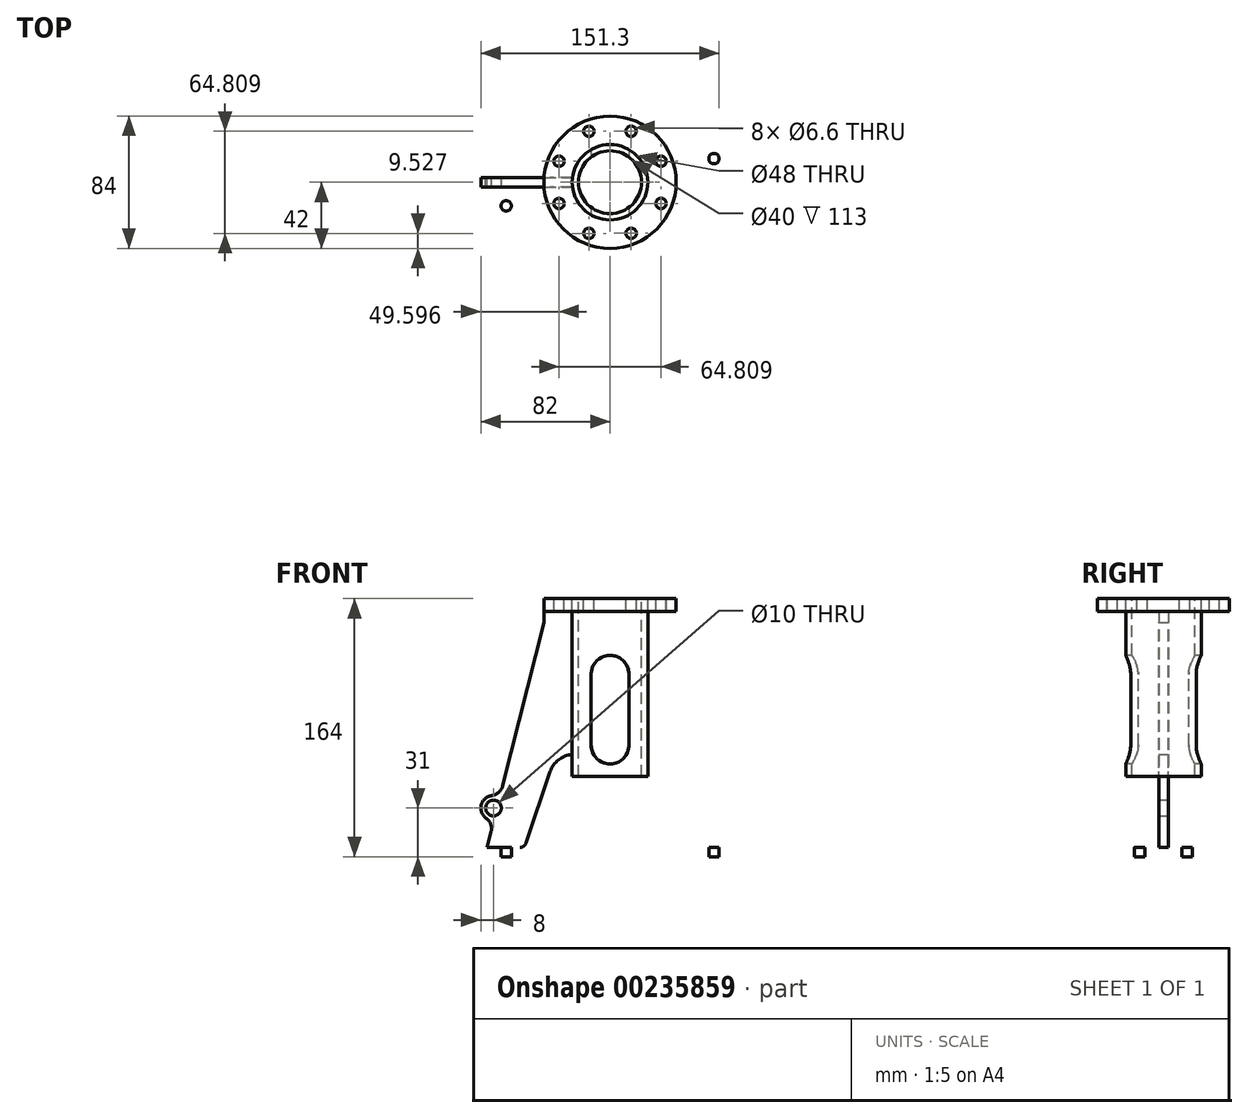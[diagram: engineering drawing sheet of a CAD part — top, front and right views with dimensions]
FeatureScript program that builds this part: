
annotation { "Feature Type Name" : "Feature", "Feature Type Description" : "" }
export const myFeature = defineFeature(function(context is Context, id is Id, definition is map)
    precondition{}
    {
        {
            var Q0;
            Q0=qCreatedBy(makeId("Front.planeOp"),FACE);
            var sketch = newSketch(context, id + "F0", { "sketchPlane" : qUnion([Q0])});
            skLineSegment(sketch, "E0.0", {"start": v(-42, 0) * mm, "end": v(-42, -8) * mm});
            skLineSegment(sketch, "E1.0", {"start": v(42, 0) * mm, "end": v(42, -8) * mm});
            skLineSegment(sketch, "E2", {"start": v(-42, 0) * mm, "end": v(42, 0) * mm});
            skLineSegment(sketch, "E3.0", {"start": v(-42, -8) * mm, "end": v(42, -8) * mm});
            skLineSegment(sketch, "E4", {"start": v(0, 0) * mm, "end": v(0, -4.96) * mm});
            skLineSegment(sketch, "E5", {"start": v(-78, -158) * mm, "end": v(-75.5, -148) * mm});
            skLineSegment(sketch, "E6.trimOffspring", {"start": v(-78, -158) * mm, "end": v(-78, -164) * mm});
            skCircle(sketch, "E7", {"center": v(-74, -133) * mm, "radius": 5 * mm});
            skArc(sketch, "E8", {"start": v(-75, -125.06) * mm, "mid": v(-81.76, -131.05) * mm, "end": v(-78.63, -139.53) * mm});
            skLineSegment(sketch, "E9.trimOffspring", {"start": v(-68.24, -119.08) * mm, "end": v(-42, -15) * mm});
            skPoint(sketch, "E10.visualSharp", {"position": v(-70, -126.07) * mm});
            skArc(sketch, "E10.filletArc", {"start": v(-75, -125.06) * mm, "mid": v(-70.7, -123.12) * mm, "end": v(-68.24, -119.08) * mm});
            skPoint(sketch, "E11.visualSharp", {"position": v(-73.73, -141) * mm});
            skArc(sketch, "E11.filletArc", {"start": v(-75.5, -148) * mm, "mid": v(-75.75, -143.28) * mm, "end": v(-78.63, -139.53) * mm});
            skArc(sketch, "E12", {"start": v(0, -36) * mm, "mid": v(-8.49, -39.51) * mm, "end": v(-12, -48) * mm});
            skArc(sketch, "E13", {"start": v(-12, -93) * mm, "mid": v(-8.49, -101.49) * mm, "end": v(0, -105) * mm});
            skLineSegment(sketch, "E14.0", {"start": v(-12, -48) * mm, "end": v(-12, -93) * mm});
            skLineSegment(sketch, "E15", {"start": v(-24, -8) * mm, "end": v(-24, -113) * mm});
            skLineSegment(sketch, "E16", {"start": v(0, -105) * mm, "end": v(0, -113) * mm});
            skLineSegment(sketch, "E17.0", {"start": v(-20, -8) * mm, "end": v(-20, -113) * mm});
            skPoint(sketch, "E18.visualSharp", {"position": v(-50, -164) * mm});
            skLineSegment(sketch, "E19", {"start": v(-78, -164) * mm, "end": v(-57.17, -164) * mm});
            skLineSegment(sketch, "E20", {"start": v(0, -113) * mm, "end": v(-24, -113) * mm});
            skLineSegment(sketch, "E21", {"start": v(-47.7, -157.21) * mm, "end": v(-32.3, -111.79) * mm});
            skArc(sketch, "E22.filletArc", {"start": v(-57.17, -164) * mm, "mid": v(-51.34, -162.13) * mm, "end": v(-47.7, -157.21) * mm});
            skPoint(sketch, "E23.visualSharp", {"position": v(-30, -105) * mm});
            skArc(sketch, "E23.filletArc", {"start": v(-22.83, -105) * mm, "mid": v(-28.66, -106.87) * mm, "end": v(-32.3, -111.79) * mm});
            skArc(sketch, "E24.0", {"start": v(-22.83, -99) * mm, "mid": v(-32.15, -102) * mm, "end": v(-37.98, -109.86) * mm});
            skLineSegment(sketch, "E24.1", {"start": v(-53.38, -155.28) * mm, "end": v(-37.98, -109.86) * mm});
            skArc(sketch, "E24.2", {"start": v(-57.17, -158) * mm, "mid": v(-54.84, -157.25) * mm, "end": v(-53.38, -155.28) * mm});
            skLineSegment(sketch, "E24.3", {"start": v(-78, -158) * mm, "end": v(-57.17, -158) * mm});
            skLineSegment(sketch, "E25.MirrorCS", {"start": v(78, -158) * mm, "end": v(78, -164) * mm});
            skArc(sketch, "E26.MirrorCS", {"start": v(75, -125.06) * mm, "mid": v(70.7, -123.12) * mm, "end": v(68.24, -119.08) * mm});
            skArc(sketch, "E27.MirrorCS", {"start": v(75.5, -148) * mm, "mid": v(75.75, -143.28) * mm, "end": v(78.63, -139.53) * mm});
            skArc(sketch, "E28.MirrorCS", {"start": v(57.17, -158) * mm, "mid": v(54.84, -157.25) * mm, "end": v(53.38, -155.28) * mm});
            skLineSegment(sketch, "E29.MirrorCS", {"start": v(78, -158) * mm, "end": v(75.5, -148) * mm});
            skArc(sketch, "E30.MirrorCS", {"start": v(57.17, -164) * mm, "mid": v(51.34, -162.13) * mm, "end": v(47.7, -157.21) * mm});
            skArc(sketch, "E31.MirrorCS", {"start": v(22.83, -105) * mm, "mid": v(28.66, -106.87) * mm, "end": v(32.3, -111.79) * mm});
            skArc(sketch, "E32.MirrorCS", {"start": v(22.83, -99) * mm, "mid": v(32.15, -102) * mm, "end": v(37.98, -109.86) * mm});
            skCircle(sketch, "E33.MirrorC", {"center": v(74, -133) * mm, "radius": 5 * mm});
            skPoint(sketch, "E34.MirrorP", {"position": v(50, -164) * mm});
            skPoint(sketch, "E35.MirrorP", {"position": v(30, -105) * mm});
            skLineSegment(sketch, "E36.MirrorCS", {"start": v(53.38, -155.28) * mm, "end": v(37.98, -109.86) * mm});
            skLineSegment(sketch, "E37.MirrorCS", {"start": v(78, -158) * mm, "end": v(57.17, -158) * mm});
            skLineSegment(sketch, "E38.MirrorCS", {"start": v(0, -113) * mm, "end": v(24, -113) * mm});
            skPoint(sketch, "E39.MirrorP", {"position": v(70, -126.07) * mm});
            skLineSegment(sketch, "E40.MirrorCS", {"start": v(68.24, -119.08) * mm, "end": v(42, -15) * mm});
            skLineSegment(sketch, "E41.MirrorCS", {"start": v(78, -164) * mm, "end": v(57.17, -164) * mm});
            skLineSegment(sketch, "E42.MirrorCS", {"start": v(12, -48) * mm, "end": v(12, -93) * mm});
            skLineSegment(sketch, "E43.MirrorCS", {"start": v(47.7, -157.21) * mm, "end": v(32.3, -111.79) * mm});
            skLineSegment(sketch, "E44.MirrorCS", {"start": v(24, -8) * mm, "end": v(24, -113) * mm});
            skPoint(sketch, "E45.MirrorP", {"position": v(73.73, -141) * mm});
            skArc(sketch, "E46.MirrorCS", {"start": v(75, -125.06) * mm, "mid": v(81.76, -131.05) * mm, "end": v(78.63, -139.53) * mm});
            skArc(sketch, "E47.MirrorCS", {"start": v(0, -36) * mm, "mid": v(8.49, -39.51) * mm, "end": v(12, -48) * mm});
            skLineSegment(sketch, "E48.MirrorCS", {"start": v(20, -8) * mm, "end": v(20, -113) * mm});
            skArc(sketch, "E49.MirrorCS", {"start": v(12, -93) * mm, "mid": v(8.49, -101.49) * mm, "end": v(0, -105) * mm});
            skLineSegment(sketch, "E50.MirrorCS", {"start": v(-42, -8) * mm, "end": v(-42, -15) * mm});
            skLineSegment(sketch, "E51", {"start": v(42, -8) * mm, "end": v(42, -15) * mm});
            skLineSegment(sketch, "E52", {"start": v(-22.83, -99) * mm, "end": v(-10.4, -99) * mm});
            skLineSegment(sketch, "E53", {"start": v(22.83, -105) * mm, "end": v(-22.83, -105) * mm});
            skLineSegment(sketch, "E54.trimOffspring", {"start": v(10.4, -99) * mm, "end": v(22.83, -99) * mm});
            skSolve(sketch);
        }
        {
            var Q0;
            Q0=qCreatedBy(makeId("Top.planeOp"),FACE);
            var sketch = newSketch(context, id + "F1", { "sketchPlane" : qUnion([Q0])});
            skCircle(sketch, "E55", {"center": v(0, 0) * mm, "radius": 42 * mm});
            skCircle(sketch, "E56", {"center": v(0, 0) * mm, "radius": 20 * mm});
            skCircle(sketch, "E57", {"center": v(0, 0) * mm, "radius": 24 * mm});
            skCircle(sketch, "E58", {"center": v(0, 0) * mm, "radius": 35 * mm, "construction": true});
            skLineSegment(sketch, "E59", {"start": v(0, 0) * mm, "end": v(30.78, 74.31) * mm, "construction": true});
            skCircle(sketch, "E60", {"center": v(13.4, 32.34) * mm, "radius": 3.3 * mm});
            skCircle(sketch, "E61.1.0", {"center": v(-13.44, 32.32) * mm, "radius": 3.3 * mm});
            skCircle(sketch, "E61.2.0", {"center": v(-32.4, 13.33) * mm, "radius": 3.3 * mm});
            skCircle(sketch, "E61.3.0", {"center": v(-32.38, -13.51) * mm, "radius": 3.3 * mm});
            skCircle(sketch, "E61.4.0", {"center": v(-13.4, -32.47) * mm, "radius": 3.3 * mm});
            skCircle(sketch, "E61.5.0", {"center": v(13.44, -32.45) * mm, "radius": 3.3 * mm});
            skCircle(sketch, "E61.6.0", {"center": v(32.4, -13.46) * mm, "radius": 3.3 * mm});
            skCircle(sketch, "E61.7.0", {"center": v(32.38, 13.37) * mm, "radius": 3.3 * mm});
            skPoint(sketch, "E61.center", {"position": v(0, -0.07) * mm});
            skSolve(sketch);
        }
        {
            var Q0;
            Q0=makeQuery(id+"F0.imprint","IMPRINT",FACE,{"disambiguationData":[TD([[makeQuery(id+"F0.imprint","IMPRINT",EDGE,{"derivedFrom":sQuery(id+"F0.wireOp",EDGE,"E6.trimOffspring")}),1.0]])]});
            var Q1;
            Q1=makeQuery(id+"F0.imprint","IMPRINT",FACE,{"disambiguationData":[TD([[makeQuery(id+"F0.imprint","IMPRINT",EDGE,{"derivedFrom":sQuery(id+"F0.wireOp",EDGE,"E25.MirrorCS")}),-1.0]])]});
            var Q2;
            {var subQ3=sQuery(id+"F0.wireOp",EDGE,"E15");var subQ6=sQuery(id+"F0.wireOp",EDGE,"E23.filletArc");var subQ8=makeQuery(id+"F0.imprint","INTERSECT",VERTEX,{"derivedFrom":[subQ3,subQ6]});Q2=makeQuery(id+"F0.imprint","IMPRINT",FACE,{"disambiguationData":[TD([[makeQuery(id+"F0.imprint","IMPRINT",EDGE,{"disambiguationData":[TD([[subQ8,1.0]])],"derivedFrom":subQ3}),1.0]])]});}
            var Q3;
            {var subQ3=sQuery(id+"F0.wireOp",EDGE,"E52");var subQ5=sQuery(id+"F0.wireOp",EDGE,"E17.0");var subQ6=makeQuery(id+"F0.imprint","INTERSECT",VERTEX,{"derivedFrom":[subQ5,subQ3]});Q3=makeQuery(id+"F0.imprint","IMPRINT",FACE,{"disambiguationData":[TD([[makeQuery(id+"F0.imprint","IMPRINT",EDGE,{"disambiguationData":[TD([[subQ6,-1.0]])],"derivedFrom":subQ5}),1.0]])]});}
            var Q4;
            {var subQ0=sQuery(id+"F0.wireOp",EDGE,"E54.trimOffspring");var subQ1=sQuery(id+"F0.wireOp",EDGE,"E48.MirrorCS");var subQ2=makeQuery(id+"F0.imprint","INTERSECT",VERTEX,{"derivedFrom":[subQ1,subQ0]});Q4=makeQuery(id+"F0.imprint","IMPRINT",FACE,{"disambiguationData":[TD([[makeQuery(id+"F0.imprint","IMPRINT",EDGE,{"disambiguationData":[TD([[subQ2,-1.0]])],"derivedFrom":subQ1}),-1.0]])]});}
            var Q5;
            {var subQ3=sQuery(id+"F0.wireOp",EDGE,"E53");var subQ9=sQuery(id+"F0.wireOp",EDGE,"E31.MirrorCS");var subQ11=makeQuery(id+"F0.imprint","INTERSECT",VERTEX,{"derivedFrom":[subQ9,subQ3]});Q5=makeQuery(id+"F0.imprint","IMPRINT",FACE,{"disambiguationData":[TD([[makeQuery(id+"F0.imprint","IMPRINT",EDGE,{"disambiguationData":[TD([[subQ11,-1.0]])],"derivedFrom":subQ9}),1.0]])]});}
            extrude(context, id + "F2", {"entities" : qUnion([Q0, Q1, Q2, Q3, Q4, Q5]), "depth" : 60 * mm, "symmetric" : true});
        }
        {
            var Q0;
            {var subQ3=sQuery(id+"F0.wireOp",EDGE,"E15");var subQ6=sQuery(id+"F0.wireOp",EDGE,"E3.0");var subQ9=makeQuery(id+"F0.imprint","INTERSECT",VERTEX,{"derivedFrom":[subQ6,subQ3]});Q0=makeQuery(id+"F0.imprint","IMPRINT",FACE,{"disambiguationData":[TD([[makeQuery(id+"F0.imprint","IMPRINT",EDGE,{"disambiguationData":[TD([[subQ9,-1.0]])],"derivedFrom":subQ6}),-1.0]])]});}
            var Q1;
            {var subQ3=sQuery(id+"F0.wireOp",EDGE,"E15");var subQ6=sQuery(id+"F0.wireOp",EDGE,"E23.filletArc");var subQ8=makeQuery(id+"F0.imprint","INTERSECT",VERTEX,{"derivedFrom":[subQ3,subQ6]});Q1=makeQuery(id+"F0.imprint","IMPRINT",FACE,{"disambiguationData":[TD([[makeQuery(id+"F0.imprint","IMPRINT",EDGE,{"disambiguationData":[TD([[subQ8,1.0]])],"derivedFrom":subQ3}),1.0]])]});}
            var Q2;
            {var subQ3=sQuery(id+"F0.wireOp",EDGE,"E15");var subQ7=sQuery(id+"F0.wireOp",EDGE,"E20");var subQ8=makeQuery(id+"F0.imprint","INTERSECT",VERTEX,{"derivedFrom":[subQ3,subQ7]});Q2=makeQuery(id+"F0.imprint","IMPRINT",FACE,{"disambiguationData":[TD([[makeQuery(id+"F0.imprint","IMPRINT",EDGE,{"disambiguationData":[TD([[subQ8,1.0]])],"derivedFrom":subQ3}),1.0]])]});}
            var Q3;
            Q3=sQuery(id+"F0.wireOp",EDGE,"E4");
            revolve(context, id + "F3", {"entities" : qUnion([Q0, Q1, Q2]), "axis" : qUnion([Q3]), "revolveType" : RevolveType.FULL});
        }
        {
            var Q0;
            Q0=qCreatedBy(makeId("Top.planeOp"),FACE);
            var sketch = newSketch(context, id + "F4", { "sketchPlane" : qUnion([Q0])});
            skLineSegment(sketch, "E62.0", {"start": v(-78, 0) * mm, "end": v(-78, 30) * mm});
            skLineSegment(sketch, "E62.1", {"start": v(-78, 0) * mm, "end": v(-78, -30) * mm});
            skLineSegment(sketch, "E63.0", {"start": v(78, 0) * mm, "end": v(78, 30) * mm});
            skLineSegment(sketch, "E63.1", {"start": v(78, 0) * mm, "end": v(78, -30) * mm});
            skLineSegment(sketch, "E64.0", {"start": v(0, -30) * mm, "end": v(78, -30) * mm});
            skLineSegment(sketch, "E64.1", {"start": v(-78, -30) * mm, "end": v(0, -30) * mm});
            skLineSegment(sketch, "E65.0", {"start": v(0, 30) * mm, "end": v(78, 30) * mm});
            skLineSegment(sketch, "E65.1", {"start": v(-78, 30) * mm, "end": v(0, 30) * mm});
            skLineSegment(sketch, "E66.0", {"start": v(-78, 15) * mm, "end": v(0, 15) * mm, "construction": true});
            skLineSegment(sketch, "E67.MirrorCS", {"start": v(-78, -15) * mm, "end": v(0, -15) * mm, "construction": true});
            skLineSegment(sketch, "E68.MirrorCS", {"start": v(78, 15) * mm, "end": v(0, 15) * mm, "construction": true});
            skLineSegment(sketch, "E69.MirrorCS", {"start": v(78, -15) * mm, "end": v(0, -15) * mm, "construction": true});
            skCircle(sketch, "E70", {"center": v(-66, 15) * mm, "radius": 3.3 * mm});
            skCircle(sketch, "E71.MirrorC", {"center": v(-66, -15) * mm, "radius": 3.3 * mm});
            skCircle(sketch, "E72.MirrorC", {"center": v(66, 15) * mm, "radius": 3.3 * mm});
            skCircle(sketch, "E73.MirrorC", {"center": v(66, -15) * mm, "radius": 3.3 * mm});
            skCircle(sketch, "E74", {"center": v(0, 0) * mm, "radius": 24 * mm});
            skLineSegment(sketch, "E75", {"start": v(-60.56, 30) * mm, "end": v(-21.28, 11.1) * mm});
            skLineSegment(sketch, "E76.MirrorCS", {"start": v(-60.56, -30) * mm, "end": v(-21.28, -11.1) * mm});
            skLineSegment(sketch, "E77.MirrorCS", {"start": v(60.56, 30) * mm, "end": v(21.28, 11.1) * mm});
            skLineSegment(sketch, "E78.MirrorCS", {"start": v(60.56, -30) * mm, "end": v(21.28, -11.1) * mm});
            skCircle(sketch, "E79", {"center": v(0, 0) * mm, "radius": 20 * mm});
            skSolve(sketch);
        }
        {
            var Q0;
            {var subQ0=sQuery(id+"F4.wireOp",EDGE,"E75");Q0=makeQuery(id+"F4.imprint","IMPRINT",FACE,{"disambiguationData":[TD([[makeQuery(id+"F4.imprint","IMPRINT",EDGE,{"derivedFrom":subQ0}),1.0]])]});}
            var Q1;
            {var subQ0=sQuery(id+"F4.wireOp",EDGE,"E76.MirrorCS");Q1=makeQuery(id+"F4.imprint","IMPRINT",FACE,{"disambiguationData":[TD([[makeQuery(id+"F4.imprint","IMPRINT",EDGE,{"derivedFrom":subQ0}),-1.0]])]});}
            var Q2;
            Q2=makeQuery(id+"F4.imprint","IMPRINT",FACE,{"disambiguationData":[TD([[makeQuery(id+"F4.imprint","IMPRINT",EDGE,{"derivedFrom":sQuery(id+"F4.wireOp",EDGE,"E70")}),1.0]])]});
            var Q3;
            Q3=makeQuery(id+"F4.imprint","IMPRINT",FACE,{"disambiguationData":[TD([[makeQuery(id+"F4.imprint","IMPRINT",EDGE,{"derivedFrom":sQuery(id+"F4.wireOp",EDGE,"E71.MirrorC")}),-1.0]])]});
            var Q4;
            Q4=makeQuery(id+"F4.imprint","IMPRINT",FACE,{"disambiguationData":[TD([[makeQuery(id+"F4.imprint","IMPRINT",EDGE,{"derivedFrom":sQuery(id+"F4.wireOp",EDGE,"E72.MirrorC")}),-1.0]])]});
            var Q5;
            Q5=makeQuery(id+"F4.imprint","IMPRINT",FACE,{"disambiguationData":[TD([[makeQuery(id+"F4.imprint","IMPRINT",EDGE,{"derivedFrom":sQuery(id+"F4.wireOp",EDGE,"E73.MirrorC")}),1.0]])]});
            var Q6;
            Q6=makeQuery(id+"F4.imprint","IMPRINT",FACE,{"disambiguationData":[TD([[makeQuery(id+"F4.imprint","IMPRINT",EDGE,{"derivedFrom":sQuery(id+"F4.wireOp",EDGE,"E79")}),-1.0]])]});
            var Q7;
            Q7=makeQuery(id+"F4.imprint","IMPRINT",FACE,{"disambiguationData":[TD([[makeQuery(id+"F4.imprint","IMPRINT",EDGE,{"derivedFrom":sQuery(id+"F4.wireOp",EDGE,"E79")}),1.0]])]});
            extrude(context, id + "F5", {"entities" : qUnion([Q0, Q1, Q2, Q3, Q4, Q5, Q6, Q7]), "operationType" : NewBodyOperationType.REMOVE, "oppositeDirection" : true, "depth" : 200 * mm});
        }
        {
            var Q0;
            Q0=makeQuery(id+"F4.imprint","IMPRINT",FACE,{"disambiguationData":[TD([[makeQuery(id+"F4.imprint","IMPRINT",EDGE,{"derivedFrom":sQuery(id+"F4.wireOp",EDGE,"E79")}),-1.0]])]});
            extrude(context, id + "F6", {"entities" : qUnion([Q0]), "oppositeDirection" : true, "depth" : 113 * mm});
        }
        {
            var Q0;
            Q0=makeQuery(id+"F0.imprint","IMPRINT",FACE,{"disambiguationData":[TD([[makeQuery(id+"F0.imprint","IMPRINT",EDGE,{"derivedFrom":sQuery(id+"F0.wireOp",EDGE,"E5")}),-1.0]])]});
            var Q1;
            Q1=makeQuery(id+"F0.imprint","IMPRINT",FACE,{"disambiguationData":[TD([[makeQuery(id+"F0.imprint","IMPRINT",EDGE,{"derivedFrom":sQuery(id+"F0.wireOp",EDGE,"E26.MirrorCS")}),1.0]])]});
            extrude(context, id + "F7", {"entities" : qUnion([Q0, Q1]), "depth" : 6 * mm, "symmetric" : true});
        }
        {
            var Q0;
            Q0=makeQuery(id+"F0.imprint","IMPRINT",FACE,{"disambiguationData":[TD([[makeQuery(id+"F0.imprint","IMPRINT",EDGE,{"derivedFrom":sQuery(id+"F0.wireOp",EDGE,"E12")}),1.0]])]});
            extrude(context, id + "F8", {"entities" : qUnion([Q0]), "operationType" : NewBodyOperationType.REMOVE, "oppositeDirection" : true, "depth" : 90 * mm, "symmetric" : true});
        }
        {
            var Q0;
            Q0=makeQuery(id+"F1.imprint","IMPRINT",FACE,{"disambiguationData":[TD([[makeQuery(id+"F1.imprint","IMPRINT",EDGE,{"derivedFrom":sQuery(id+"F1.wireOp",EDGE,"E55")}),1.0]])]});
            extrude(context, id + "F9", {"entities" : qUnion([Q0]), "oppositeDirection" : true, "depth" : 8 * mm});
        }
    });
